# Revit family: Haworth_ActiveComponents_HeightAdjusTable_Rectangular_BUILD
name_source: partatom
category: Furniture Systems
revit_build: Autodesk Revit Architecture 2015 (Build: 20141119_1515(x64)
units: mm (PartAtom-declared; Revit-internal decimal feet)

## types (4) — shared parameters
Actual Height = 29"
Assembly Code = E2020200
Custom Size = No
Description = Haworth - Active Components - Rectangular Height Adjustable Table
Height = 29"
Leg Height = 27 13/16"
Manufacturer = Haworth
Max. Depth = 29"
Max. Height = 35"
Max. Width = 70"
Min. Depth = 23"
Min. Height = 22"
Min. Width = 58"
Model = TAYN
Radius = 3"
Rail Finish = Haworth _ Paint _ Black
Revision Number = 1
Size = Verify Final Dim. w/ Haworth
Thickness = 1 3/16"
URL = www.haworth.com
URL - Product = https://www.haworth.com
Warranty = https://www.haworth.com

## per-type parameters (varying)
| type | 23 Deep | Actual Depth | Actual Width | Depth | Leg Front Offset | Leg Offset | Width |
| 29d 70w | No | 29" | 70" | 29" | 19 5/16" | 28 11/16" | 70" |
| 29d 58w | No | 29" | 58" | 29" | 19 5/16" | 22 11/16" | 58" |
| 23d 58w | Yes | 23" | 58" | 23" | 16 5/16" | 22 11/16" | 58" |
| 23d 70w | Yes | 23" | 70" | 23" | 16 5/16" | 28 11/16" | 70" |

## geometry (parser evidence)
native form markers: Blend x82, Sweep x10
no freeform markers — native parametric forms only
